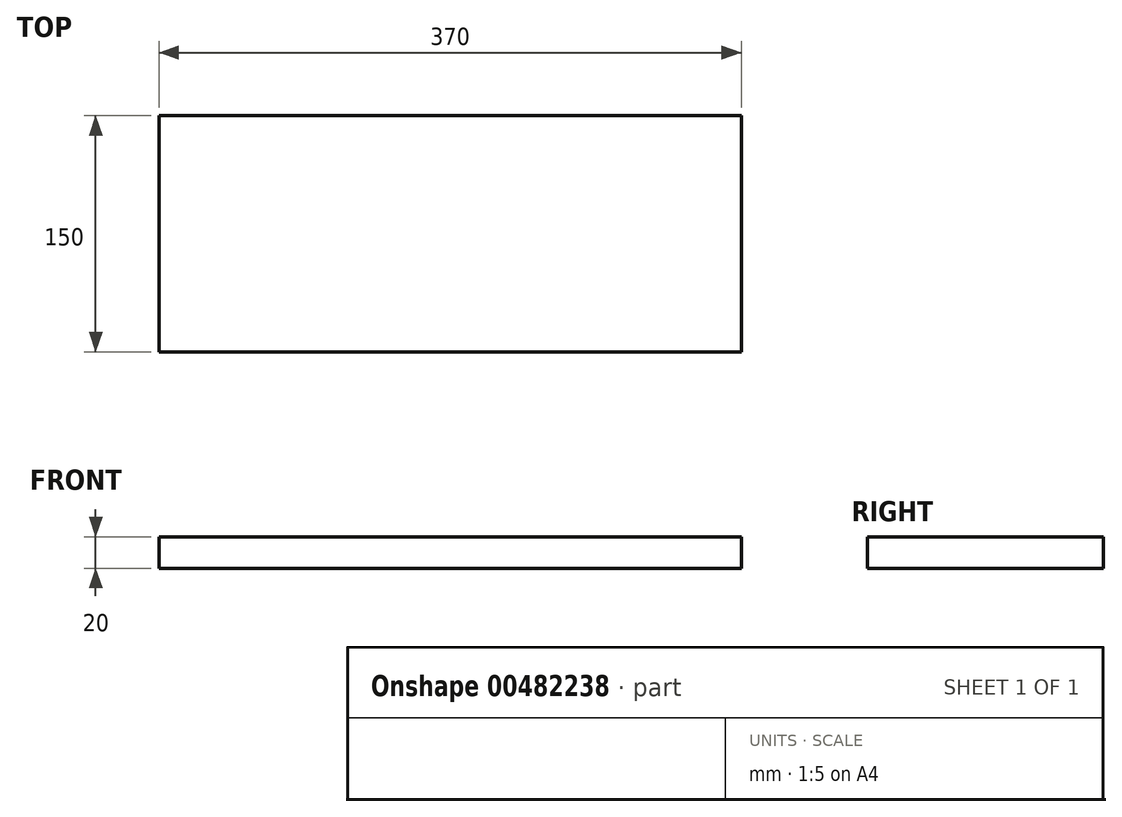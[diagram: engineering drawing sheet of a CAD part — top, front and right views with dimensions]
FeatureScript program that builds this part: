
annotation { "Feature Type Name" : "Feature", "Feature Type Description" : "" }
export const myFeature = defineFeature(function(context is Context, id is Id, definition is map)
    precondition{}
    {
        {
            var Q0;
            Q0=qCreatedBy(makeId("Right.planeOp"),FACE);
            var sketch = newSketch(context, id + "F0", { "sketchPlane" : qUnion([Q0])});
            skLineSegment(sketch, "E0.bottom", {"start": v(-75, 10) * mm, "end": v(75, 10) * mm});
            skLineSegment(sketch, "E0.top", {"start": v(-75, -10) * mm, "end": v(75, -10) * mm});
            skLineSegment(sketch, "E0.left", {"start": v(-75, 10) * mm, "end": v(-75, -10) * mm});
            skLineSegment(sketch, "E0.right", {"start": v(75, 10) * mm, "end": v(75, -10) * mm});
            skPoint(sketch, "E0.middle", {"position": v(0, 0) * mm});
            skSolve(sketch);
        }
        {
            var Q0;
            Q0 = qSketchRegion(id + "F0", true);
            extrude(context, id + "F1", {"entities" : qUnion([Q0]), "depth" : 370 * mm});
        }
    });
